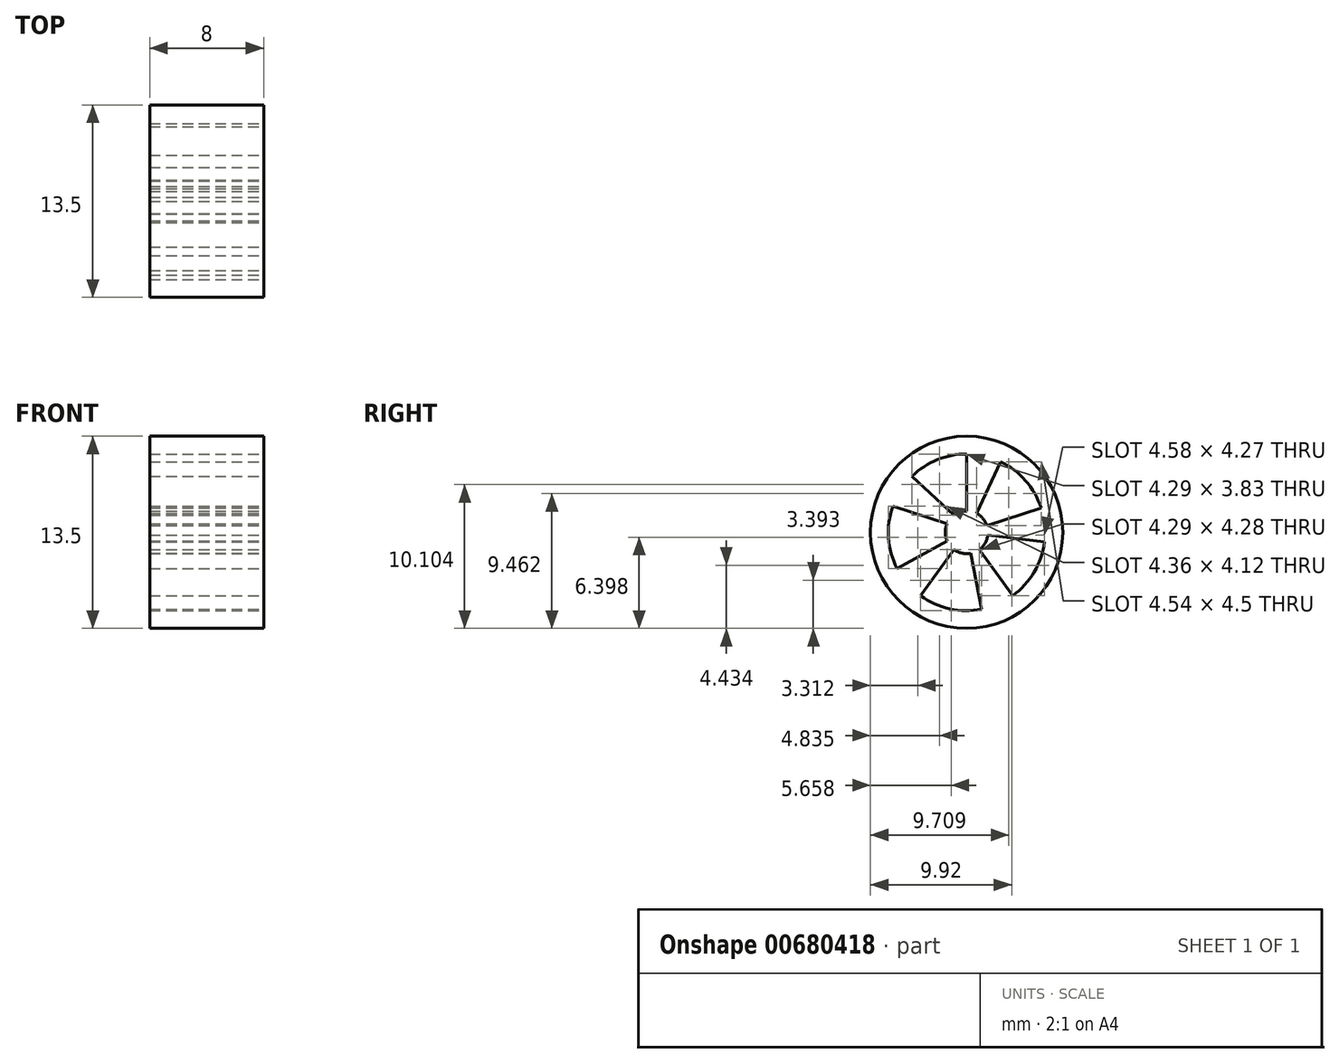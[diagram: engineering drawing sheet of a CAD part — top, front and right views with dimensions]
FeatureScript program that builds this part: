
annotation { "Feature Type Name" : "Feature", "Feature Type Description" : "" }
export const myFeature = defineFeature(function(context is Context, id is Id, definition is map)
    precondition{}
    {
        {
            var Q0;
            Q0=qCreatedBy(makeId("Right.planeOp"),FACE);
            var sketch = newSketch(context, id + "F0", { "sketchPlane" : qUnion([Q0])});
            skCircle(sketch, "E0", {"center": v(0, 0) * mm, "radius": 6.75 * mm});
            skSolve(sketch);
        }
        {
            var Q0;
            Q0=qSketchRegion(id+"F0",true);
            var Q1;
            Q1=makeQuery(id+"F0.imprint","IMPRINT",FACE,{"disambiguationData":[TD([[makeQuery(id+"F0.imprint","IMPRINT",EDGE,{"derivedFrom":sQuery(id+"F0.wireOp",EDGE,"E0")}),1.0]])]});
            extrude(context, id + "F1", {"entities" : qUnion([Q0, Q1]), "depth" : 8 * mm, "offsetDistance" : 25 * mm});
        }
        {
            var Q0;
            Q0=makeQuery(id+"F1.opExtrude","CAP_FACE",FACE,{"disambiguationData":[OSD([sQuery(id+"F0.wireOp",EDGE,"E0")])],"isStart":false});
            var sketch = newSketch(context, id + "F2", { "sketchPlane" : qUnion([Q0])});
            skCircle(sketch, "E1", {"center": v(0, 0) * mm, "radius": 5.5 * mm});
            skCircle(sketch, "E2", {"center": v(0, 0) * mm, "radius": 1.5 * mm});
            skLineSegment(sketch, "E3", {"start": v(0, 1.5) * mm, "end": v(0, 5.5) * mm});
            skLineSegment(sketch, "E4", {"start": v(0.69, 1.33) * mm, "end": v(2.38, 4.96) * mm});
            skLineSegment(sketch, "E5", {"start": v(1.49, -0.18) * mm, "end": v(5.46, -0.67) * mm});
            skLineSegment(sketch, "E6", {"start": v(0.88, -1.21) * mm, "end": v(3.23, -4.45) * mm});
            skLineSegment(sketch, "E7", {"start": v(0.29, -1.47) * mm, "end": v(1.05, -5.4) * mm});
            skLineSegment(sketch, "E8", {"start": v(-0.88, -1.21) * mm, "end": v(-3.23, -4.45) * mm});
            skLineSegment(sketch, "E9", {"start": v(-1.38, 0.6) * mm, "end": v(-5.19, 1.83) * mm});
            skLineSegment(sketch, "E10", {"start": v(-0.94, 5.42) * mm, "end": v(-0.95, 5.26) * mm});
            skLineSegment(sketch, "E11", {"start": v(1.43, 0.46) * mm, "end": v(5.23, 1.7) * mm});
            skLineSegment(sketch, "E12", {"start": v(-3.83, 3.95) * mm, "end": v(-0.9, 1.2) * mm});
            skLineSegment(sketch, "E13", {"start": v(-4.88, -2.53) * mm, "end": v(-1.38, -0.6) * mm});
            skSolve(sketch);
        }
        {
            var Q0;
            {var subQ0=sQuery(id+"F2.wireOp",EDGE,"E3");Q0=makeQuery(id+"F2.imprint","IMPRINT",FACE,{"disambiguationData":[TD([[makeQuery(id+"F2.imprint","IMPRINT",EDGE,{"derivedFrom":subQ0}),1.0]])]});}
            var Q1;
            {var subQ0=sQuery(id+"F2.wireOp",EDGE,"E4");Q1=makeQuery(id+"F2.imprint","IMPRINT",FACE,{"disambiguationData":[TD([[makeQuery(id+"F2.imprint","IMPRINT",EDGE,{"derivedFrom":subQ0}),-1.0]])]});}
            var Q2;
            {var subQ0=sQuery(id+"F2.wireOp",EDGE,"E5");Q2=makeQuery(id+"F2.imprint","IMPRINT",FACE,{"disambiguationData":[TD([[makeQuery(id+"F2.imprint","IMPRINT",EDGE,{"derivedFrom":subQ0}),-1.0]])]});}
            var Q3;
            {var subQ0=sQuery(id+"F2.wireOp",EDGE,"E7");Q3=makeQuery(id+"F2.imprint","IMPRINT",FACE,{"disambiguationData":[TD([[makeQuery(id+"F2.imprint","IMPRINT",EDGE,{"derivedFrom":subQ0}),-1.0]])]});}
            var Q4;
            {var subQ0=sQuery(id+"F2.wireOp",EDGE,"E9");Q4=makeQuery(id+"F2.imprint","IMPRINT",FACE,{"disambiguationData":[TD([[makeQuery(id+"F2.imprint","IMPRINT",EDGE,{"derivedFrom":subQ0}),1.0]])]});}
            extrude(context, id + "F3", {"entities" : qUnion([Q0, Q1, Q2, Q3, Q4]), "operationType" : NewBodyOperationType.REMOVE, "oppositeDirection" : true, "depth" : 25 * mm, "offsetDistance" : 25 * mm});
        }
    });
